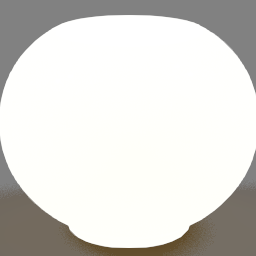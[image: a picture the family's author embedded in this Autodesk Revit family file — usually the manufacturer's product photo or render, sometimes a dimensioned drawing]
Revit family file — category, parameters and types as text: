
# Revit family: 3-090X-xx Castore Mirror
name_source: partatom
category: Luminarias
units: mm (PartAtom-declared; Revit-internal decimal feet)

## family parameters
Anfitrión = Muro
Compartido = No
Corte con vacíos al cargar = No
Cota de conector redondo = Diámetro de uso
Número OmniClass = 23.80.70.00
Origen de luz = No
Punto de cálculo de habitación = No
Siempre vertical = Sí
Tipo de pieza = Normal
Título OmniClass = Lighting

## types (3) — shared parameters
Diffuser = Ghost Mirror
Fabricante = Vanita by Oxygen
Height = 800 mm  [stored 2.62467 ft]
Lámpara = LED Array
Metal Finish 1 = 15 - Black
Modelo = 3-090X-xx / Castore
References = Ref. 3 = 120 V / Ref. 37 = 277 V
URL = www.oxygenlighting.com
Voltage = 120 V
Voltage Input = 120 V or 277 V - 50/60 Hz
zero-valued in all types: Elevación por defecto

## per-type parameters (varying)
| type | Comentarios de vataje | Width |
| 3-0901-15 / Black | 1 x 46.8 W at 120 V | 500 mm  [stored 1.64042 ft] |
| 3-0903-15 / Black | 1 x 77.9 W at 120 V | 800 mm  [stored 2.62467 ft] |
| 3-0902-15 / Black | 1 x 59.1 W at 120 V | 600 mm  [stored 1.9685 ft] |

note: [stored X ft] marks values corroborated as IEEE doubles in the binary element streams (Revit-internal decimal feet)

## geometry (parser evidence)
native form markers: Sweep x5
no freeform markers — native parametric forms only
